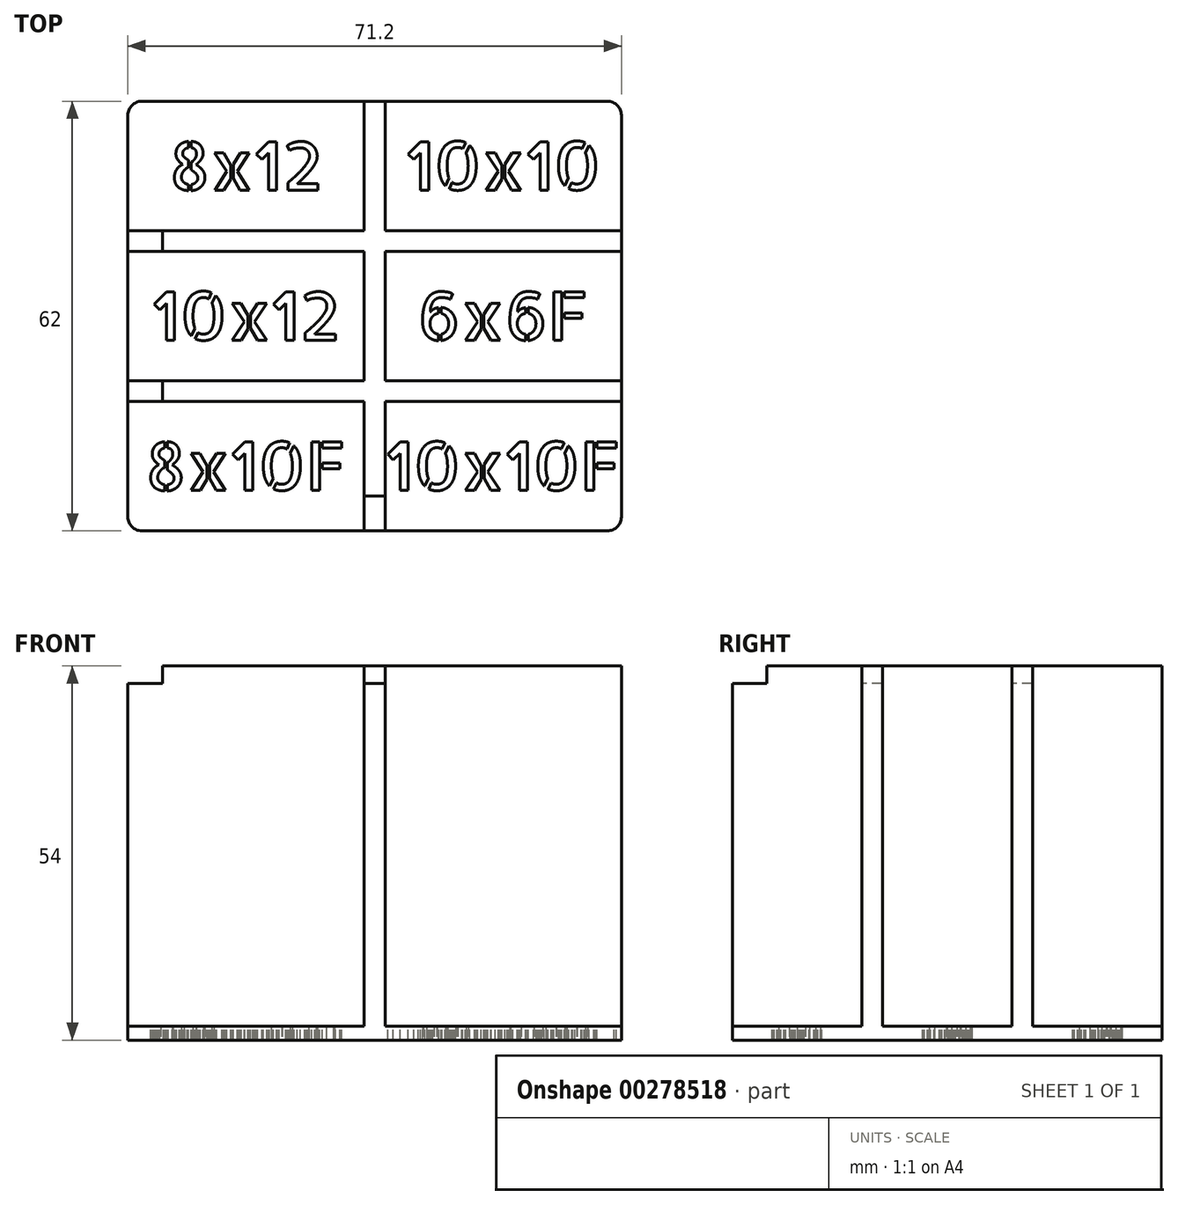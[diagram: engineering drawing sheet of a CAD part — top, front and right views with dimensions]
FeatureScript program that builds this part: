
annotation { "Feature Type Name" : "Feature", "Feature Type Description" : "" }
export const myFeature = defineFeature(function(context is Context, id is Id, definition is map)
    precondition{}
    {
        {
            var Q0;
            Q0=qCreatedBy(makeId("Top.planeOp"),FACE);
            var sketch = newSketch(context, id + "F0", { "sketchPlane" : qUnion([Q0])});
            skLineSegment(sketch, "E0.bottom", {"start": v(-35.6, 31) * mm, "end": v(35.6, 31) * mm});
            skLineSegment(sketch, "E0.top", {"start": v(-35.6, -31) * mm, "end": v(35.6, -31) * mm});
            skLineSegment(sketch, "E0.left", {"start": v(-35.6, 31) * mm, "end": v(-35.6, -31) * mm});
            skLineSegment(sketch, "E0.right", {"start": v(35.6, 31) * mm, "end": v(35.6, -31) * mm});
            skSolve(sketch);
        }
        {
            var Q0;
            Q0=qSketchRegion(id+"F0",true);
            extrude(context, id + "F1", {"entities" : qUnion([Q0]), "depth" : 2 * mm});
        }
        {
            var Q0;
            Q0=makeQuery(id+"F1.opExtrude","CAP_FACE",FACE,{"disambiguationData":[OSD([sQuery(id+"F0.wireOp",EDGE,"E0.bottom"),sQuery(id+"F0.wireOp",EDGE,"E0.top"),sQuery(id+"F0.wireOp",EDGE,"E0.left"),sQuery(id+"F0.wireOp",EDGE,"E0.right")])],"isStart":false});
            var sketch = newSketch(context, id + "F2", { "sketchPlane" : qUnion([Q0])});
            skLineSegment(sketch, "E1", {"start": v(-1.5, 31) * mm, "end": v(1.5, 31) * mm});
            skLineSegment(sketch, "E2", {"start": v(1.5, 12.33) * mm, "end": v(1.5, 31) * mm});
            skLineSegment(sketch, "E3", {"start": v(1.5, 12.33) * mm, "end": v(35.6, 12.33) * mm});
            skLineSegment(sketch, "E4", {"start": v(35.6, 12.33) * mm, "end": v(35.6, 9.33) * mm});
            skLineSegment(sketch, "E5", {"start": v(35.6, 9.33) * mm, "end": v(1.5, 9.33) * mm});
            skLineSegment(sketch, "E6", {"start": v(1.5, 9.33) * mm, "end": v(1.5, -9.33) * mm});
            skLineSegment(sketch, "E7", {"start": v(1.5, -9.33) * mm, "end": v(35.6, -9.33) * mm});
            skLineSegment(sketch, "E8", {"start": v(35.6, -9.33) * mm, "end": v(35.6, -12.33) * mm});
            skLineSegment(sketch, "E9", {"start": v(35.6, -12.33) * mm, "end": v(1.5, -12.33) * mm});
            skLineSegment(sketch, "E10", {"start": v(1.5, -12.33) * mm, "end": v(1.5, -31) * mm});
            skLineSegment(sketch, "E11", {"start": v(1.5, -31) * mm, "end": v(-1.5, -31) * mm});
            skLineSegment(sketch, "E12", {"start": v(-1.5, -31) * mm, "end": v(-1.5, -12.33) * mm});
            skLineSegment(sketch, "E13", {"start": v(-1.5, -12.33) * mm, "end": v(-35.6, -12.33) * mm});
            skLineSegment(sketch, "E14", {"start": v(-35.6, -12.33) * mm, "end": v(-35.6, -9.33) * mm});
            skLineSegment(sketch, "E15", {"start": v(-35.6, -9.33) * mm, "end": v(-1.5, -9.33) * mm});
            skLineSegment(sketch, "E16", {"start": v(-1.5, -9.33) * mm, "end": v(-1.5, 9.33) * mm});
            skLineSegment(sketch, "E17", {"start": v(-1.5, 9.33) * mm, "end": v(-35.6, 9.33) * mm});
            skLineSegment(sketch, "E18", {"start": v(-35.6, 9.33) * mm, "end": v(-35.6, 12.33) * mm});
            skLineSegment(sketch, "E19", {"start": v(-35.6, 12.33) * mm, "end": v(-1.5, 12.33) * mm});
            skLineSegment(sketch, "E20", {"start": v(-1.5, 12.33) * mm, "end": v(-1.5, 31) * mm});
            skSolve(sketch);
        }
        {
            var Q0;
            Q0=qSketchRegion(id+"F2",true);
            extrude(context, id + "F3", {"entities" : qUnion([Q0]), "operationType" : NewBodyOperationType.ADD, "depth" : 52 * mm});
        }
        {
            var Q0;
            Q0=makeQuery(id+"F1.opExtrude","CAP_FACE",FACE,{"disambiguationData":[OSD([sQuery(id+"F0.wireOp",EDGE,"E0.bottom"),sQuery(id+"F0.wireOp",EDGE,"E0.top"),sQuery(id+"F0.wireOp",EDGE,"E0.left"),sQuery(id+"F0.wireOp",EDGE,"E0.right")])],"isStart":false});
            var sketch = newSketch(context, id + "F4", { "sketchPlane" : qUnion([Q0])});
            skText(sketch, "E21", { "text": "8x12", "fontName": "AllertaStencil-Regular.ttf"});
            skLineSegment(sketch, "E22", {"start": v(-35.6, 21.67) * mm, "end": v(35.6, 21.67) * mm, "construction": true});
            skLineSegment(sketch, "E23", {"start": v(-35.6, 0) * mm, "end": v(35.6, 0) * mm, "construction": true});
            skLineSegment(sketch, "E24", {"start": v(-35.6, -21.67) * mm, "end": v(35.6, -21.67) * mm, "construction": true});
            skLineSegment(sketch, "E25", {"start": v(-18.55, -31) * mm, "end": v(-18.55, 31) * mm, "construction": true});
            skLineSegment(sketch, "E26", {"start": v(18.55, -31) * mm, "end": v(18.55, 31) * mm, "construction": true});
            skText(sketch, "E27", { "text": "10x10", "fontName": "AllertaStencil-Regular.ttf"});
            skText(sketch, "E28", { "text": "10x12", "fontName": "AllertaStencil-Regular.ttf"});
            skText(sketch, "E29", { "text": "6x6F", "fontName": "AllertaStencil-Regular.ttf"});
            skText(sketch, "E30", { "text": "8x10F", "fontName": "AllertaStencil-Regular.ttf"});
            skText(sketch, "E31", { "text": "10x10F", "fontName": "AllertaStencil-Regular.ttf"});
            const initialGuessF4  = {"E21": [-0.02958, 0.01817, 1, 0, 0.007], "E27": [0.00458, 0.01817, 1, 0, 0.007], "E28": [-0.03208, -0.0035, 1, 0, 0.007], "E29": [0.00622, -0.0035, 1, 0, 0.007], "E30": [-0.033, -0.02517, 1, 0, 0.007], "E31": [0.0016, -0.02517, 1, 0, 0.007]};
            skSetInitialGuess(sketch, initialGuessF4);
            skSolve(sketch);
        }
        {
            var Q0;
            Q0=qSketchRegion(id+"F4",true);
            var Q1;
            Q1=makeQuery(id+"F1.opExtrude","CAP_FACE",FACE,{"disambiguationData":[OSD([sQuery(id+"F0.wireOp",EDGE,"E0.bottom"),sQuery(id+"F0.wireOp",EDGE,"E0.top"),sQuery(id+"F0.wireOp",EDGE,"E0.left"),sQuery(id+"F0.wireOp",EDGE,"E0.right")])],"isStart":true});
            extrude(context, id + "F5", {"entities" : qUnion([Q0]), "operationType" : NewBodyOperationType.REMOVE, "endBound" : BoundingType.UP_TO_SURFACE, "oppositeDirection" : true, "endBoundEntityFace" : qUnion([Q1]), "depth" : 25 * mm});
        }
        {
            var Q0;
            Q0=makeQuery(id+"F1.opExtrude","SWEPT_EDGE",EDGE,{"disambiguationData":[OSD([sQuery(id+"F0.wireOp",EDGE,"E0.top"),sQuery(id+"F0.wireOp",EDGE,"E0.left")])]});
            var Q1;
            Q1=makeQuery(id+"F1.opExtrude","SWEPT_EDGE",EDGE,{"disambiguationData":[OSD([sQuery(id+"F0.wireOp",EDGE,"E0.bottom"),sQuery(id+"F0.wireOp",EDGE,"E0.left")])]});
            var Q2;
            Q2=makeQuery(id+"F1.opExtrude","SWEPT_EDGE",EDGE,{"disambiguationData":[OSD([sQuery(id+"F0.wireOp",EDGE,"E0.top"),sQuery(id+"F0.wireOp",EDGE,"E0.right")])]});
            var Q3;
            Q3=makeQuery(id+"F1.opExtrude","SWEPT_EDGE",EDGE,{"disambiguationData":[OSD([sQuery(id+"F0.wireOp",EDGE,"E0.bottom"),sQuery(id+"F0.wireOp",EDGE,"E0.right")])]});
            fillet(context, id + "F6", {"entities" : qUnion([Q0, Q1, Q2, Q3]), "radius" : 2 * mm, "tangentPropagation" : true, "allowEdgeOverflow" : false});
        }
        {
            var Q0;
            Q0=makeQuery(id+"F3.opExtrude","CAP_FACE",FACE,{"disambiguationData":[OSD([sQuery(id+"F2.wireOp",EDGE,"E1"),sQuery(id+"F2.wireOp",EDGE,"E2"),sQuery(id+"F2.wireOp",EDGE,"E3"),sQuery(id+"F2.wireOp",EDGE,"E4"),sQuery(id+"F2.wireOp",EDGE,"E5"),sQuery(id+"F2.wireOp",EDGE,"E6"),sQuery(id+"F2.wireOp",EDGE,"E7"),sQuery(id+"F2.wireOp",EDGE,"E8"),sQuery(id+"F2.wireOp",EDGE,"E9"),sQuery(id+"F2.wireOp",EDGE,"E10"),sQuery(id+"F2.wireOp",EDGE,"E11"),sQuery(id+"F2.wireOp",EDGE,"E12"),sQuery(id+"F2.wireOp",EDGE,"E13"),sQuery(id+"F2.wireOp",EDGE,"E14"),sQuery(id+"F2.wireOp",EDGE,"E15"),sQuery(id+"F2.wireOp",EDGE,"E16"),sQuery(id+"F2.wireOp",EDGE,"E17"),sQuery(id+"F2.wireOp",EDGE,"E18"),sQuery(id+"F2.wireOp",EDGE,"E19"),sQuery(id+"F2.wireOp",EDGE,"E20")])],"isStart":false});
            var sketch = newSketch(context, id + "F7", { "sketchPlane" : qUnion([Q0])});
            skLineSegment(sketch, "E32.bottom", {"start": v(-1.5, -31) * mm, "end": v(1.5, -31) * mm});
            skLineSegment(sketch, "E32.top", {"start": v(-1.5, -26) * mm, "end": v(1.5, -26) * mm});
            skLineSegment(sketch, "E32.left", {"start": v(-1.5, -31) * mm, "end": v(-1.5, -26) * mm});
            skLineSegment(sketch, "E32.right", {"start": v(1.5, -31) * mm, "end": v(1.5, -26) * mm});
            skLineSegment(sketch, "E33.bottom", {"start": v(-35.6, 12.33) * mm, "end": v(-30.6, 12.33) * mm});
            skLineSegment(sketch, "E33.top", {"start": v(-35.6, 9.33) * mm, "end": v(-30.6, 9.33) * mm});
            skLineSegment(sketch, "E33.left", {"start": v(-35.6, 12.33) * mm, "end": v(-35.6, 9.33) * mm});
            skLineSegment(sketch, "E33.right", {"start": v(-30.6, 12.33) * mm, "end": v(-30.6, 9.33) * mm});
            skLineSegment(sketch, "E34.bottom", {"start": v(-35.6, -9.33) * mm, "end": v(-30.6, -9.33) * mm});
            skLineSegment(sketch, "E34.top", {"start": v(-35.6, -12.33) * mm, "end": v(-30.6, -12.33) * mm});
            skLineSegment(sketch, "E34.left", {"start": v(-35.6, -9.33) * mm, "end": v(-35.6, -12.33) * mm});
            skLineSegment(sketch, "E34.right", {"start": v(-30.6, -9.33) * mm, "end": v(-30.6, -12.33) * mm});
            skPoint(sketch, "E35.top.end.orphan", {"position": v(30.6, 9.33) * mm});
            skPoint(sketch, "E36.top.end.orphan", {"position": v(30.6, -12.33) * mm});
            skSolve(sketch);
        }
        {
            var Q0;
            Q0=qSketchRegion(id+"F7",true);
            extrude(context, id + "F8", {"entities" : qUnion([Q0]), "operationType" : NewBodyOperationType.REMOVE, "oppositeDirection" : true, "depth" : 2.5 * mm});
        }
    });
